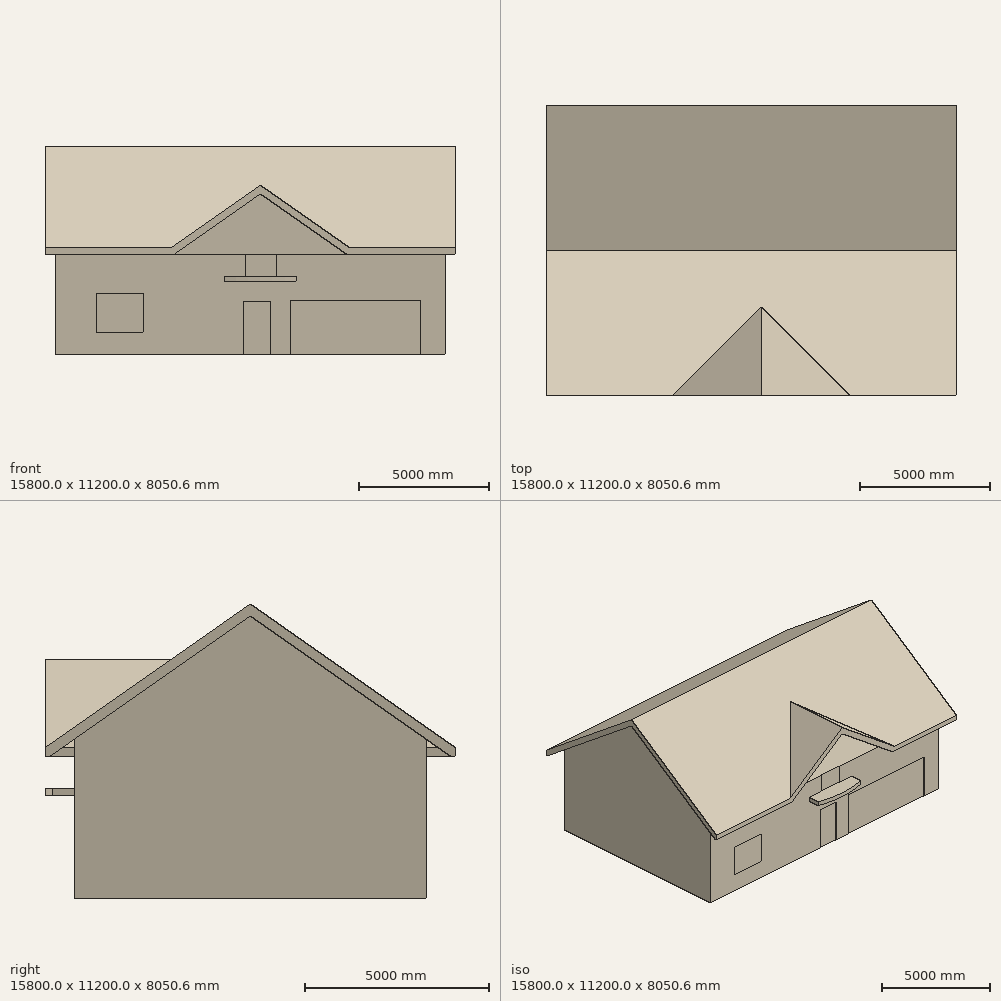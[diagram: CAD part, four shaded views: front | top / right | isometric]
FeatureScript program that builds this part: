
annotation { "Feature Type Name" : "Feature", "Feature Type Description" : "" }
export const myFeature = defineFeature(function(context is Context, id is Id, definition is map)
    precondition{}
    {
        {
            var Q0;
            Q0=qCreatedBy(makeId("Top.planeOp"),FACE);
            var sketch = newSketch(context, id + "F0", { "sketchPlane" : qUnion([Q0])});
            skLineSegment(sketch, "E0.bottom", {"start": v(0, 0) * mm, "end": v(15000, 0) * mm});
            skLineSegment(sketch, "E0.top", {"start": v(0, 9600) * mm, "end": v(15000, 9600) * mm});
            skLineSegment(sketch, "E0.left", {"start": v(0, 0) * mm, "end": v(0, 9600) * mm});
            skLineSegment(sketch, "E0.right", {"start": v(15000, 0) * mm, "end": v(15000, 9600) * mm});
            skLineSegment(sketch, "E1.0", {"start": v(440, 440) * mm, "end": v(440, 9160) * mm});
            skLineSegment(sketch, "E1.1", {"start": v(440, 440) * mm, "end": v(14560, 440) * mm});
            skLineSegment(sketch, "E1.2", {"start": v(14560, 440) * mm, "end": v(14560, 9160) * mm});
            skLineSegment(sketch, "E1.3", {"start": v(440, 9160) * mm, "end": v(14560, 9160) * mm});
            skLineSegment(sketch, "E2.bottom", {"start": v(4670, 9160) * mm, "end": v(4910, 9160) * mm});
            skLineSegment(sketch, "E2.top", {"start": v(4670, 440) * mm, "end": v(4910, 440) * mm});
            skLineSegment(sketch, "E2.left", {"start": v(4670, 9160) * mm, "end": v(4670, 440) * mm});
            skLineSegment(sketch, "E2.right", {"start": v(4910, 9160) * mm, "end": v(4910, 440) * mm});
            skLineSegment(sketch, "E3.bottom", {"start": v(8320, 9160) * mm, "end": v(8560, 9160) * mm});
            skLineSegment(sketch, "E3.top", {"start": v(8320, 440) * mm, "end": v(8560, 440) * mm});
            skLineSegment(sketch, "E3.left", {"start": v(8320, 9160) * mm, "end": v(8320, 440) * mm});
            skLineSegment(sketch, "E3.right", {"start": v(8560, 9160) * mm, "end": v(8560, 440) * mm});
            skLineSegment(sketch, "E4", {"start": v(8560, 6440) * mm, "end": v(14560, 6440) * mm});
            skLineSegment(sketch, "E5", {"start": v(7233, 0) * mm, "end": v(7233, 440) * mm});
            skLineSegment(sketch, "E6", {"start": v(8283, 440) * mm, "end": v(8283, 0) * mm});
            skLineSegment(sketch, "E7", {"start": v(7803.8, 440) * mm, "end": v(7803.8, 0) * mm});
            skSolve(sketch);
        }
        {
            var Q0;
            Q0=qCreatedBy(makeId("Top.planeOp"),FACE);
            var sketch = newSketch(context, id + "F1", { "sketchPlane" : qUnion([Q0])});
            skLineSegment(sketch, "E8.bottom", {"start": v(440, 440) * mm, "end": v(4790, 440) * mm});
            skLineSegment(sketch, "E8.top", {"start": v(440, 4247.62) * mm, "end": v(4790, 4247.62) * mm});
            skLineSegment(sketch, "E8.left", {"start": v(440, 440) * mm, "end": v(440, 4247.62) * mm});
            skLineSegment(sketch, "E8.right", {"start": v(4790, 440) * mm, "end": v(4790, 4247.62) * mm});
            skLineSegment(sketch, "E9.bottom", {"start": v(4910, 440) * mm, "end": v(6770, 440) * mm});
            skLineSegment(sketch, "E9.top", {"start": v(4910, 3831.16) * mm, "end": v(6770, 3831.16) * mm});
            skLineSegment(sketch, "E9.left", {"start": v(4910, 440) * mm, "end": v(4910, 3831.16) * mm});
            skLineSegment(sketch, "E9.right", {"start": v(6770, 440) * mm, "end": v(6770, 3831.16) * mm});
            skLineSegment(sketch, "E10.bottom", {"start": v(6890, 440) * mm, "end": v(10440, 440) * mm});
            skLineSegment(sketch, "E10.top", {"start": v(6890, 3771.67) * mm, "end": v(10440, 3771.67) * mm});
            skLineSegment(sketch, "E10.left", {"start": v(6890, 440) * mm, "end": v(6890, 3771.67) * mm});
            skLineSegment(sketch, "E10.right", {"start": v(10440, 440) * mm, "end": v(10440, 3771.67) * mm});
            skLineSegment(sketch, "E11.bottom", {"start": v(14560, 440) * mm, "end": v(10560, 440) * mm});
            skLineSegment(sketch, "E11.top", {"start": v(14560, 3632.85) * mm, "end": v(10560, 3632.85) * mm});
            skLineSegment(sketch, "E11.left", {"start": v(14560, 440) * mm, "end": v(14560, 3632.85) * mm});
            skLineSegment(sketch, "E11.right", {"start": v(10560, 440) * mm, "end": v(10560, 3632.85) * mm});
            skSolve(sketch);
        }
        {
            var Q0;
            Q0=qCreatedBy(makeId("Right.planeOp"),FACE);
            var sketch = newSketch(context, id + "F2", { "sketchPlane" : qUnion([Q0])});
            skLineSegment(sketch, "E12.bottom", {"start": v(0, 0) * mm, "end": v(9600, 0) * mm});
            skLineSegment(sketch, "E12.top", {"start": v(0, 4360) * mm, "end": v(9600, 4360) * mm});
            skLineSegment(sketch, "E12.left", {"start": v(0, 0) * mm, "end": v(0, 4360) * mm});
            skLineSegment(sketch, "E12.right", {"start": v(9600, 0) * mm, "end": v(9600, 4360) * mm});
            skLineSegment(sketch, "E13", {"start": v(4800, 4360) * mm, "end": v(4800, 7721) * mm});
            skLineSegment(sketch, "E14", {"start": v(4800, 7721) * mm, "end": v(0, 4360) * mm});
            skLineSegment(sketch, "E15", {"start": v(4800, 7721) * mm, "end": v(9600, 4360) * mm});
            skSolve(sketch);
        }
        {
            var Q0;
            Q0 = qSketchRegion(id + "F2", true);
            var Q1;
            Q1=sQuery(id+"F0.wireOp",VERTEX,"E0.right.start");
            extrude(context, id + "F3", {"entities" : qUnion([Q0]), "endBound" : BoundingType.UP_TO_VERTEX, "depth" : 25 * mm, "endBoundEntityVertex" : qUnion([Q1]), "offsetDistance" : 25 * mm});
        }
        {
            var Q0;
            Q0=makeQuery(id+"F3.opExtrude","CAP_FACE",FACE,{"disambiguationData":[OSD([sQuery(id+"F2.wireOp",EDGE,"E12.bottom"),sQuery(id+"F2.wireOp",EDGE,"E12.left"),sQuery(id+"F2.wireOp",EDGE,"E12.right"),sQuery(id+"F2.wireOp",EDGE,"E14"),sQuery(id+"F2.wireOp",EDGE,"E15")])],"isStart":true});
            var sketch = newSketch(context, id + "F4", { "sketchPlane" : qUnion([Q0])});
            skLineSegment(sketch, "E16", {"start": v(-4800, 7721) * mm, "end": v(-4800, 8050.6) * mm});
            skLineSegment(sketch, "E17", {"start": v(-4800, 8050.6) * mm, "end": v(-10400, 4129.44) * mm});
            skLineSegment(sketch, "E18", {"start": v(-10400, 4129.44) * mm, "end": v(-10400, 3882.46) * mm});
            skLineSegment(sketch, "E19", {"start": v(-10400, 3882.46) * mm, "end": v(-10282, 3882.46) * mm});
            skLineSegment(sketch, "E20", {"start": v(-10282, 3882.46) * mm, "end": v(-4800, 7721) * mm});
            skLineSegment(sketch, "E21.MirrorCS", {"start": v(-4800, 8050.6) * mm, "end": v(800, 4129.44) * mm});
            skLineSegment(sketch, "E22.MirrorCS", {"start": v(682, 3882.46) * mm, "end": v(-4800, 7721) * mm});
            skLineSegment(sketch, "E23.MirrorCS", {"start": v(800, 3882.46) * mm, "end": v(682, 3882.46) * mm});
            skLineSegment(sketch, "E24.MirrorCS", {"start": v(800, 4129.44) * mm, "end": v(800, 3882.46) * mm});
            skSolve(sketch);
        }
        {
            var Q0;
            Q0=makeQuery(id+"F3.opExtrude","SWEPT_FACE",FACE,{"disambiguationData":[OSD([sQuery(id+"F2.wireOp",EDGE,"E12.left")])]});
            var sketch = newSketch(context, id + "F5", { "sketchPlane" : qUnion([Q0])});
            skLineSegment(sketch, "E25.bottom", {"start": v(6890, 5500) * mm, "end": v(8890, 5500) * mm});
            skLineSegment(sketch, "E25.top", {"start": v(6890, 3000) * mm, "end": v(8890, 3000) * mm});
            skLineSegment(sketch, "E25.left", {"start": v(6890, 5500) * mm, "end": v(6890, 3000) * mm});
            skLineSegment(sketch, "E25.right", {"start": v(8890, 5500) * mm, "end": v(8890, 3000) * mm});
            skLineSegment(sketch, "E26", {"start": v(6890, 5500) * mm, "end": v(7890, 6200.2) * mm});
            skLineSegment(sketch, "E27", {"start": v(7890, 6200.2) * mm, "end": v(8890, 5500) * mm});
            skLineSegment(sketch, "E28", {"start": v(8890, 5500) * mm, "end": v(10518.09, 4360) * mm});
            skLineSegment(sketch, "E29", {"start": v(10518.09, 4360) * mm, "end": v(5261.91, 4360) * mm});
            skLineSegment(sketch, "E30", {"start": v(5261.91, 4360) * mm, "end": v(6890, 5500) * mm});
            skLineSegment(sketch, "E31", {"start": v(7890, 6200.2) * mm, "end": v(7890, 3000) * mm});
            skSolve(sketch);
        }
        {
            var Q0;
            Q0 = qSketchRegion(id + "F5", true);
            extrude(context, id + "F6", {"entities" : qUnion([Q0]), "operationType" : NewBodyOperationType.ADD, "endBound" : BoundingType.UP_TO_NEXT, "oppositeDirection" : true, "depth" : 25 * mm, "offsetDistance" : 25 * mm});
        }
        {
            var Q0;
            Q0 = qSketchRegion(id + "F4", true);
            extrude(context, id + "F7", {"entities" : qUnion([Q0]), "depth" : 400 * mm, "offsetDistance" : 25 * mm, "hasSecondDirection" : true, "secondDirectionOppositeDirection" : true, "secondDirectionDepth" : 15400 * mm});
        }
        {
            var Q0;
            Q0=makeQuery(id+"F6.boolean.opBoolean","MERGE",FACE,{"derivedFrom":[makeQuery(id+"F3.opExtrude","SWEPT_FACE",FACE,{"disambiguationData":[OSD([sQuery(id+"F2.wireOp",EDGE,"E12.left")])]}),makeQuery(id+"F6.opExtrude","CAP_FACE",FACE,{"disambiguationData":[OSD([sQuery(id+"F5.wireOp",EDGE,"E25.top"),sQuery(id+"F5.wireOp",EDGE,"E25.left"),sQuery(id+"F5.wireOp",EDGE,"E25.right"),sQuery(id+"F5.wireOp",EDGE,"E26"),sQuery(id+"F5.wireOp",EDGE,"E27"),sQuery(id+"F5.wireOp",EDGE,"E28"),sQuery(id+"F5.wireOp",EDGE,"E29"),sQuery(id+"F5.wireOp",EDGE,"E30")])],"isStart":true})]});
            var sketch = newSketch(context, id + "F8", { "sketchPlane" : qUnion([Q0])});
            skLineSegment(sketch, "E32", {"start": v(7890, 6200.2) * mm, "end": v(4579.91, 3882.46) * mm});
            skLineSegment(sketch, "E33", {"start": v(4579.91, 3882.46) * mm, "end": v(11200.09, 3882.46) * mm});
            skLineSegment(sketch, "E34", {"start": v(11200.09, 3882.46) * mm, "end": v(7890, 6200.2) * mm});
            skSolve(sketch);
        }
        {
            var Q0;
            Q0 = qSketchRegion(id + "F8", true);
            extrude(context, id + "F9", {"entities" : qUnion([Q0]), "operationType" : NewBodyOperationType.REMOVE, "oppositeDirection" : true, "depth" : 5220 * mm, "offsetDistance" : 25 * mm, "hasSecondDirection" : true, "secondDirectionBound" : BoundingType.THROUGH_ALL, "secondDirectionOppositeDirection" : false, "secondDirectionDepth" : 25 * mm});
        }
        {
            var Q0;
            Q0=makeQuery(id+"F6.boolean.opBoolean","MERGE",FACE,{"derivedFrom":[makeQuery(id+"F3.opExtrude","SWEPT_FACE",FACE,{"disambiguationData":[OSD([sQuery(id+"F2.wireOp",EDGE,"E12.left")])]}),makeQuery(id+"F6.opExtrude","CAP_FACE",FACE,{"disambiguationData":[OSD([sQuery(id+"F5.wireOp",EDGE,"E25.top"),sQuery(id+"F5.wireOp",EDGE,"E25.left"),sQuery(id+"F5.wireOp",EDGE,"E25.right"),sQuery(id+"F5.wireOp",EDGE,"E26"),sQuery(id+"F5.wireOp",EDGE,"E27"),sQuery(id+"F5.wireOp",EDGE,"E28"),sQuery(id+"F5.wireOp",EDGE,"E29"),sQuery(id+"F5.wireOp",EDGE,"E30")])],"isStart":true})]});
            var sketch = newSketch(context, id + "F10", { "sketchPlane" : qUnion([Q0])});
            skLineSegment(sketch, "E35", {"start": v(7890, 6200.2) * mm, "end": v(4579.91, 3882.46) * mm});
            skLineSegment(sketch, "E36", {"start": v(4579.91, 3882.46) * mm, "end": v(4456.68, 3882.46) * mm});
            skLineSegment(sketch, "E37", {"start": v(4456.68, 3882.46) * mm, "end": v(4456.68, 4129.44) * mm});
            skLineSegment(sketch, "E38", {"start": v(4456.68, 4129.44) * mm, "end": v(7890, 6533.48) * mm});
            skLineSegment(sketch, "E39", {"start": v(7890, 6533.48) * mm, "end": v(7890, 6200.2) * mm});
            skLineSegment(sketch, "E40.MirrorCS", {"start": v(11323.32, 4129.44) * mm, "end": v(7890, 6533.48) * mm});
            skLineSegment(sketch, "E41.MirrorCS", {"start": v(7890, 6200.2) * mm, "end": v(11200.09, 3882.46) * mm});
            skLineSegment(sketch, "E42.MirrorCS", {"start": v(11200.09, 3882.46) * mm, "end": v(11323.32, 3882.46) * mm});
            skLineSegment(sketch, "E43.MirrorCS", {"start": v(11323.32, 3882.46) * mm, "end": v(11323.32, 4129.44) * mm});
            skSolve(sketch);
        }
        {
            var Q0;
            Q0 = qSketchRegion(id + "F10", true);
            var Q1;
            Q1=makeQuery(id+"F7.opExtrude","SWEPT_BODY",BODY,{"disambiguationData":[OSD([sQuery(id+"F4.wireOp",EDGE,"E17"),sQuery(id+"F4.wireOp",EDGE,"E18"),sQuery(id+"F4.wireOp",EDGE,"E19"),sQuery(id+"F4.wireOp",EDGE,"E20"),sQuery(id+"F4.wireOp",EDGE,"E21.MirrorCS"),sQuery(id+"F4.wireOp",EDGE,"E22.MirrorCS"),sQuery(id+"F4.wireOp",EDGE,"E23.MirrorCS"),sQuery(id+"F4.wireOp",EDGE,"E24.MirrorCS")])]});
            var Q2;
            {var subQ0=sQuery(id+"F4.wireOp",EDGE,"E24.MirrorCS");Q2=makeQuery(id+"F9.boolean.opBoolean","SPLIT",FACE,{"disambiguationData":[TD([makeQuery(id+"F9.opExtrude","SWEPT_FACE",FACE,{"disambiguationData":[OSD([sQuery(id+"F8.wireOp",EDGE,"E32")])]})])],"derivedFrom":makeQuery(id+"F7.opExtrude","SWEPT_FACE",FACE,{"disambiguationData":[OSD([subQ0])]})});}
            extrude(context, id + "F11", {"entities" : qUnion([Q0]), "operationType" : NewBodyOperationType.ADD, "endBound" : BoundingType.UP_TO_BODY, "oppositeDirection" : true, "depth" : 25 * mm, "endBoundEntityBody" : qUnion([Q1]), "offsetDistance" : 25 * mm, "hasSecondDirection" : true, "secondDirectionBound" : BoundingType.UP_TO_SURFACE, "secondDirectionOppositeDirection" : false, "secondDirectionDepth" : 25 * mm, "secondDirectionBoundEntityFace" : qUnion([Q2])});
        }
        {
            var Q0;
            Q0=makeQuery(id+"F6.boolean.opBoolean","MERGE",FACE,{"derivedFrom":[makeQuery(id+"F3.opExtrude","SWEPT_FACE",FACE,{"disambiguationData":[OSD([sQuery(id+"F2.wireOp",EDGE,"E12.left")])]}),makeQuery(id+"F6.opExtrude","CAP_FACE",FACE,{"disambiguationData":[OSD([sQuery(id+"F5.wireOp",EDGE,"E25.top"),sQuery(id+"F5.wireOp",EDGE,"E25.left"),sQuery(id+"F5.wireOp",EDGE,"E25.right"),sQuery(id+"F5.wireOp",EDGE,"E26"),sQuery(id+"F5.wireOp",EDGE,"E27"),sQuery(id+"F5.wireOp",EDGE,"E28"),sQuery(id+"F5.wireOp",EDGE,"E29"),sQuery(id+"F5.wireOp",EDGE,"E30")])],"isStart":true})]});
            var sketch = newSketch(context, id + "F12", { "sketchPlane" : qUnion([Q0])});
            skLineSegment(sketch, "E44.bottom", {"start": v(7233, 0) * mm, "end": v(8283, 0) * mm});
            skLineSegment(sketch, "E44.top", {"start": v(7233, 2050) * mm, "end": v(8283, 2050) * mm});
            skLineSegment(sketch, "E44.left", {"start": v(7233, 0) * mm, "end": v(7233, 2050) * mm});
            skLineSegment(sketch, "E44.right", {"start": v(8283, 0) * mm, "end": v(8283, 2050) * mm});
            skLineSegment(sketch, "E45.bottom", {"start": v(1567, 2350) * mm, "end": v(3367, 2350) * mm});
            skLineSegment(sketch, "E45.top", {"start": v(1567, 850) * mm, "end": v(3367, 850) * mm});
            skLineSegment(sketch, "E45.left", {"start": v(1567, 2350) * mm, "end": v(1567, 850) * mm});
            skLineSegment(sketch, "E45.right", {"start": v(3367, 2350) * mm, "end": v(3367, 850) * mm});
            skLineSegment(sketch, "E46.bottom", {"start": v(9060, 2100) * mm, "end": v(14060, 2100) * mm});
            skLineSegment(sketch, "E46.top", {"start": v(9060, 0) * mm, "end": v(14060, 0) * mm});
            skLineSegment(sketch, "E46.left", {"start": v(9060, 2100) * mm, "end": v(9060, 0) * mm});
            skLineSegment(sketch, "E46.right", {"start": v(14060, 2100) * mm, "end": v(14060, 0) * mm});
            skLineSegment(sketch, "E47.bottom", {"start": v(7290, 3000) * mm, "end": v(8490, 3000) * mm});
            skLineSegment(sketch, "E47.top", {"start": v(7290, 5050) * mm, "end": v(8490, 5050) * mm});
            skLineSegment(sketch, "E47.left", {"start": v(7290, 3000) * mm, "end": v(7290, 5050) * mm});
            skLineSegment(sketch, "E47.right", {"start": v(8490, 3000) * mm, "end": v(8490, 5050) * mm});
            skPoint(sketch, "E48", {"position": v(7890, 5050) * mm});
            skSolve(sketch);
        }
        {
            var Q0;
            Q0 = qSketchRegion(id + "F12", true);
            extrude(context, id + "F13", {"entities" : qUnion([Q0]), "operationType" : NewBodyOperationType.REMOVE, "oppositeDirection" : true, "depth" : 25 * mm, "offsetDistance" : 25 * mm});
        }
        {
            var Q0;
            Q0=makeQuery(id+"F13.boolean.opBoolean","COPY",FACE,{"derivedFrom":makeQuery(id+"F13.opExtrude","SWEPT_FACE",FACE,{"disambiguationData":[OSD([sQuery(id+"F12.wireOp",EDGE,"E47.bottom")])]})});
            extrude(context, id + "F14", {"entities" : qUnion([Q0]), "operationType" : NewBodyOperationType.ADD, "depth" : 25 * mm, "offsetDistance" : 25 * mm});
        }
        {
            var Q0;
            Q0=makeQuery(id+"F14.opExtrude","CAP_FACE",FACE,{"disambiguationData":[OSD([sQuery(id+"F12.wireOp",EDGE,"E47.bottom")])],"isStart":false});
            var sketch = newSketch(context, id + "F15", { "sketchPlane" : qUnion([Q0])});
            skLineSegment(sketch, "E49.bottom", {"start": v(6490, 0) * mm, "end": v(9290, 0) * mm});
            skLineSegment(sketch, "E49.top", {"start": v(6490, -600) * mm, "end": v(9290, -600) * mm});
            skLineSegment(sketch, "E49.left", {"start": v(6490, 0) * mm, "end": v(6490, -600) * mm});
            skLineSegment(sketch, "E49.right", {"start": v(9290, 0) * mm, "end": v(9290, -600) * mm});
            skArc(sketch, "E50", {"start": v(6490, -600) * mm, "mid": v(7890, -800) * mm, "end": v(9290, -600) * mm});
            skSolve(sketch);
        }
        {
            var Q0;
            Q0 = qSketchRegion(id + "F15", true);
            extrude(context, id + "F16", {"entities" : qUnion([Q0]), "operationType" : NewBodyOperationType.ADD, "oppositeDirection" : true, "depth" : 200 * mm, "offsetDistance" : 25 * mm});
        }
    });
